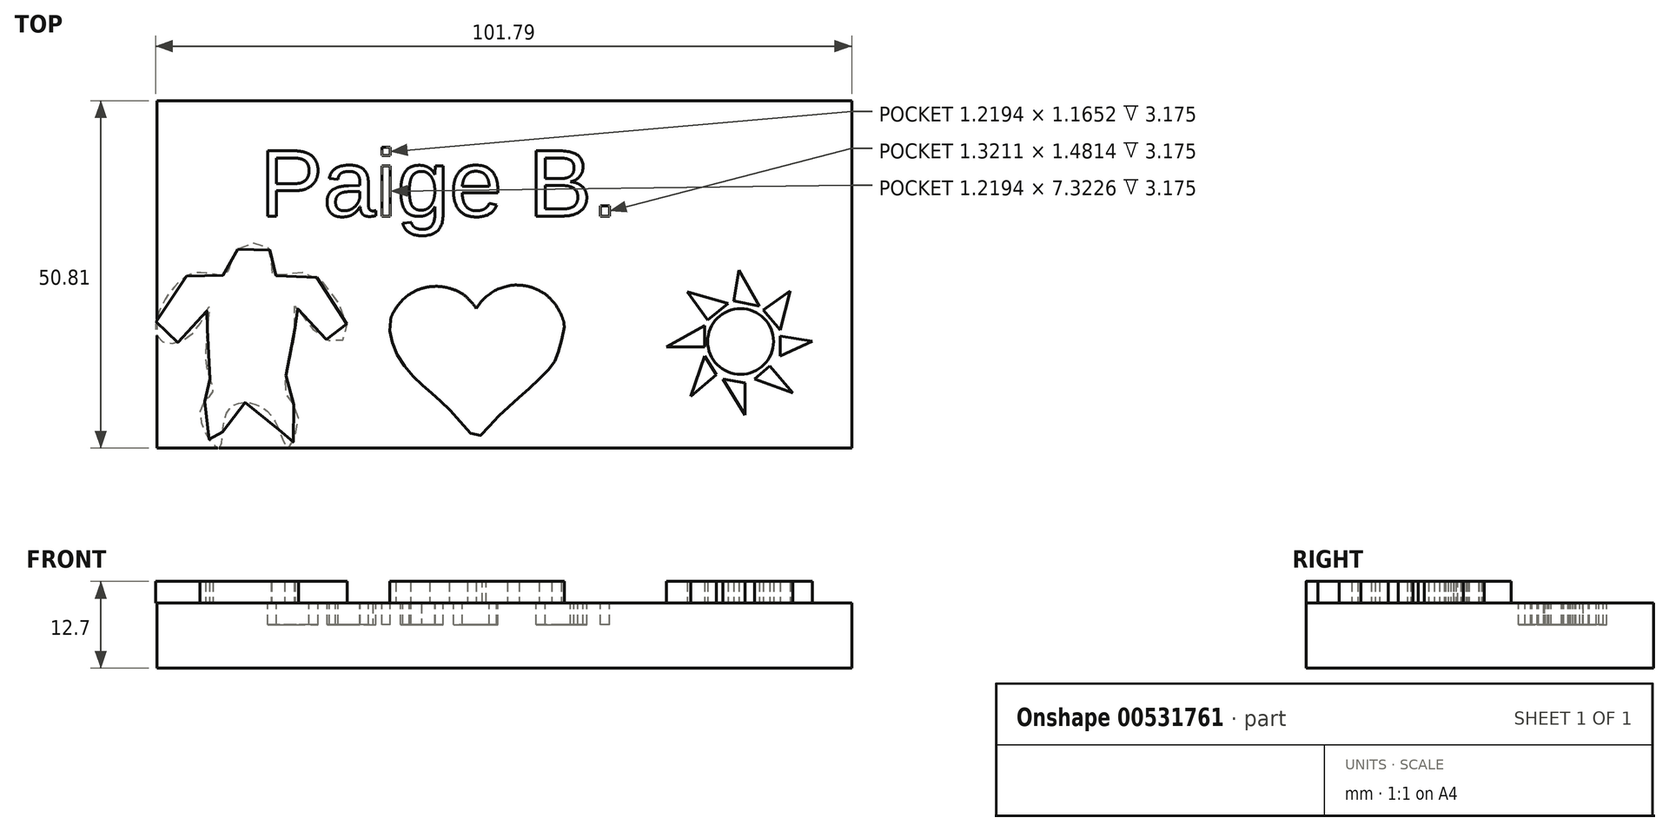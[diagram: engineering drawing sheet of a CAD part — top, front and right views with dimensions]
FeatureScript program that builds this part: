
annotation { "Feature Type Name" : "Feature", "Feature Type Description" : "" }
export const myFeature = defineFeature(function(context is Context, id is Id, definition is map)
    precondition{}
    {
        {
            var Q0;
            Q0=qCreatedBy(makeId("Top.planeOp"),FACE);
            var sketch = newSketch(context, id + "F0", { "sketchPlane" : qUnion([Q0])});
            skLineSegment(sketch, "E0.bottom", {"start": v(-50.8, 25.4) * mm, "end": v(50.8, 25.4) * mm});
            skLineSegment(sketch, "E0.top", {"start": v(-50.8, -25.4) * mm, "end": v(50.8, -25.4) * mm});
            skLineSegment(sketch, "E0.left", {"start": v(-50.8, 25.4) * mm, "end": v(-50.8, -25.4) * mm});
            skLineSegment(sketch, "E0.right", {"start": v(50.8, 25.4) * mm, "end": v(50.8, -25.4) * mm});
            skPoint(sketch, "E0.middle", {"position": v(0, 0) * mm});
            skSolve(sketch);
        }
        {
            var Q0;
            Q0=makeQuery(id+"F0.imprint","IMPRINT",FACE,{"disambiguationData":[TD([[makeQuery(id+"F0.imprint","IMPRINT",EDGE,{"derivedFrom":sQuery(id+"F0.wireOp",EDGE,"E0.bottom")}),-1.0]])]});
            extrude(context, id + "F1", {"entities" : qUnion([Q0]), "depth" : 9.52 * mm, "offsetDistance" : 25.4 * mm});
        }
        {
            var Q0;
            Q0=makeQuery(id+"F1.opExtrude","CAP_FACE",FACE,{"disambiguationData":[OSD([sQuery(id+"F0.wireOp",EDGE,"E0.bottom"),sQuery(id+"F0.wireOp",EDGE,"E0.top"),sQuery(id+"F0.wireOp",EDGE,"E0.left"),sQuery(id+"F0.wireOp",EDGE,"E0.right")])],"isStart":false});
            var sketch = newSketch(context, id + "F2", { "sketchPlane" : qUnion([Q0])});
            skPoint(sketch, "E1.4.internal.snap0", {"position": v(-50.8, -8.96) * mm});
            skPoint(sketch, "E1.15.internal.snap0", {"position": v(-50.8, -8.96) * mm});
            skPoint(sketch, "E1.17.internal.snap0", {"position": v(-23.09, -8.96) * mm});
            skFitSpline(sketch, "E1", {"points": [v(-38.94, 3.7) * mm, v(-40.8, 0) * mm, v(-45.88, 0) * mm, v(-50.8, -8.96) * mm, v(-45.88, -8.96) * mm, v(-43.1, -4.62) * mm, v(-43.57, -13.41) * mm, v(-42.64, -17.11) * mm, v(-44.5, -20.35) * mm, v(-41.72, -25.4) * mm, v(-40.33, -19.89) * mm, v(-34.32, -20.35) * mm, v(-31.54, -25.4) * mm, v(-30.16, -20.35) * mm, v(-32, -17.11) * mm, v(-30.62, -8.96) * mm, v(-30.62, -4.62) * mm, v(-26.92, -8.96) * mm, v(-23.09, -8.96) * mm, v(-28.3, 0) * mm, v(-33.86, 0) * mm, v(-34.32, 3.7) * mm, v(-38.94, 3.7) * mm]});
            skSolve(sketch);
        }
        {
            var Q0;
            {var subQ0=sQuery(id+"F2.wireOp",EDGE,"E1");var subQ1=makeQuery(id+"F1.opExtrude","CAP_EDGE",EDGE,{"disambiguationData":[OSD([sQuery(id+"F0.wireOp",EDGE,"E0.left")])],"isStart":false});var subQ2=makeQuery(id+"F2.imprint","INTERSECT",VERTEX,{"disambiguationData":[OD(0.0)],"derivedFrom":[subQ1,subQ0]});Q0=makeQuery(id+"F2.imprint","IMPRINT",FACE,{"disambiguationData":[TD([[makeQuery(id+"F2.imprint","IMPRINT",EDGE,{"disambiguationData":[TD([[subQ2,1.0]])],"derivedFrom":subQ0}),1.0]])]});}
            var Q1;
            {var subQ0=sQuery(id+"F2.wireOp",EDGE,"E1");var subQ1=makeQuery(id+"F1.opExtrude","CAP_EDGE",EDGE,{"disambiguationData":[OSD([sQuery(id+"F0.wireOp",EDGE,"E0.top")])],"isStart":false});var subQ2=makeQuery(id+"F2.imprint","INTERSECT",VERTEX,{"disambiguationData":[OD(0.0)],"derivedFrom":[subQ1,subQ0]});Q1=makeQuery(id+"F2.imprint","IMPRINT",FACE,{"disambiguationData":[TD([[makeQuery(id+"F2.imprint","IMPRINT",EDGE,{"disambiguationData":[TD([[subQ2,-1.0]])],"derivedFrom":subQ0}),1.0]])]});}
            var Q2;
            {var subQ0=sQuery(id+"F2.wireOp",EDGE,"E1");var subQ1=makeQuery(id+"F1.opExtrude","CAP_EDGE",EDGE,{"disambiguationData":[OSD([sQuery(id+"F0.wireOp",EDGE,"E0.top")])],"isStart":false});var subQ2=makeQuery(id+"F2.imprint","INTERSECT",VERTEX,{"disambiguationData":[OD(2.0)],"derivedFrom":[subQ1,subQ0]});Q2=makeQuery(id+"F2.imprint","IMPRINT",FACE,{"disambiguationData":[TD([[makeQuery(id+"F2.imprint","IMPRINT",EDGE,{"disambiguationData":[TD([[subQ2,-1.0]])],"derivedFrom":subQ0}),1.0]])]});}
            var Q3;
            {var subQ0=sQuery(id+"F2.wireOp",EDGE,"E1");var subQ1=makeQuery(id+"F1.opExtrude","CAP_EDGE",EDGE,{"disambiguationData":[OSD([sQuery(id+"F0.wireOp",EDGE,"E0.left")])],"isStart":false});var subQ5=makeQuery(id+"F2.imprint","INTERSECT",VERTEX,{"disambiguationData":[OD(0.0)],"derivedFrom":[subQ1,subQ0]});Q3=makeQuery(id+"F2.imprint","IMPRINT",FACE,{"disambiguationData":[TD([[makeQuery(id+"F2.imprint","IMPRINT",EDGE,{"disambiguationData":[TD([[subQ5,-1.0]])],"derivedFrom":subQ0}),1.0]])]});}
            extrude(context, id + "F3", {"entities" : qUnion([Q0, Q1, Q2, Q3]), "operationType" : NewBodyOperationType.ADD, "depth" : 3.17 * mm, "offsetDistance" : 25.4 * mm});
        }
        {
            var Q0;
            {var subQ0=sQuery(id+"F0.wireOp",EDGE,"E0.left");var subQ1=makeQuery(id+"F1.opExtrude","SWEPT_FACE",FACE,{"disambiguationData":[OSD([subQ0])]});var subQ2=sQuery(id+"F0.wireOp",EDGE,"E0.top");var subQ3=makeQuery(id+"F1.opExtrude","SWEPT_FACE",FACE,{"disambiguationData":[OSD([subQ2])]});var subQ4=sQuery(id+"F0.wireOp",EDGE,"E0.right");var subQ5=makeQuery(id+"F1.opExtrude","SWEPT_FACE",FACE,{"disambiguationData":[OSD([subQ4])]});var subQ6=sQuery(id+"F0.wireOp",EDGE,"E0.bottom");var subQ7=makeQuery(id+"F1.opExtrude","SWEPT_FACE",FACE,{"disambiguationData":[OSD([subQ6])]});var subQ8=sQuery(id+"F2.wireOp",EDGE,"E1");var subQ9=makeQuery(id+"F3.opExtrude","SWEPT_FACE",FACE,{"disambiguationData":[OSD([subQ8])]});var subQ10=makeQuery(id+"F3.opExtrude","CAP_FACE",FACE,{"disambiguationData":[OSD([subQ8])],"isStart":true});var subQ11=sQuery(id+"F7vCEPkGthSsVVi_1.wireOp",EDGE,"900b0a7b-35fd-46bd-af1a-971b247ca61f");Q0=makeQuery(id+"FpG3tMiEOksPE03_1.boolean.opBoolean","SPLIT",FACE,{"disambiguationData":[TD([subQ7,subQ3,subQ1,subQ5,subQ9,subQ10,makeQuery(id+"FpG3tMiEOksPE03_1.opExtrude","SWEPT_FACE",FACE,{"disambiguationData":[OSD([subQ11])]}),makeQuery(id+"FpG3tMiEOksPE03_1.opExtrude","CAP_FACE",FACE,{"disambiguationData":[OSD([subQ2,subQ11])],"isStart":true}),makeQuery(id+"FpG3tMiEOksPE03_1.opExtrude","SWEPT_FACE",FACE,{"disambiguationData":[OSD([subQ2])]})])],"derivedFrom":makeQuery(id+"F3.boolean.opBoolean","SPLIT",FACE,{"disambiguationData":[TD([subQ7,subQ3,subQ1,subQ5,subQ9,subQ10])],"derivedFrom":makeQuery(id+"F1.opExtrude","CAP_FACE",FACE,{"disambiguationData":[OSD([subQ6,subQ2,subQ0,subQ4])],"isStart":false})})});}
            var sketch = newSketch(context, id + "F4", { "sketchPlane" : qUnion([Q0])});
            skText(sketch, "E2", { "text": "Paige B.", "fontName": "Arimo-Regular.ttf"});
            const initialGuessF4  = {"E2": [-0.03574, 0.00853, 1, 0, 0.00998]};
            skSetInitialGuess(sketch, initialGuessF4);
            skSolve(sketch);
        }
        {
            var Q0;
            Q0 = qSketchRegion(id + "F4", true);
            extrude(context, id + "F5", {"entities" : qUnion([Q0]), "operationType" : NewBodyOperationType.REMOVE, "oppositeDirection" : true, "depth" : 3.17 * mm, "offsetDistance" : 25.4 * mm});
        }
        {
            var Q0;
            {var subQ0=sQuery(id+"F0.wireOp",EDGE,"E0.right");var subQ1=makeQuery(id+"F1.opExtrude","SWEPT_FACE",FACE,{"disambiguationData":[OSD([subQ0])]});var subQ2=sQuery(id+"F0.wireOp",EDGE,"E0.left");var subQ3=makeQuery(id+"F1.opExtrude","SWEPT_FACE",FACE,{"disambiguationData":[OSD([subQ2])]});var subQ4=sQuery(id+"F0.wireOp",EDGE,"E0.top");var subQ5=makeQuery(id+"F1.opExtrude","SWEPT_FACE",FACE,{"disambiguationData":[OSD([subQ4])]});var subQ6=sQuery(id+"F0.wireOp",EDGE,"E0.bottom");var subQ7=makeQuery(id+"F1.opExtrude","SWEPT_FACE",FACE,{"disambiguationData":[OSD([subQ6])]});var subQ8=sQuery(id+"F2.wireOp",EDGE,"E1");var subQ9=makeQuery(id+"F3.opExtrude","SWEPT_FACE",FACE,{"disambiguationData":[OSD([subQ8])]});var subQ10=makeQuery(id+"F3.opExtrude","CAP_FACE",FACE,{"disambiguationData":[OSD([subQ8])],"isStart":true});var subQ11=sQuery(id+"F7vCEPkGthSsVVi_1.wireOp",EDGE,"900b0a7b-35fd-46bd-af1a-971b247ca61f");var subQ12=makeQuery(id+"FpG3tMiEOksPE03_1.opExtrude","SWEPT_FACE",FACE,{"disambiguationData":[OSD([subQ11])]});var subQ13=makeQuery(id+"FpG3tMiEOksPE03_1.opExtrude","CAP_FACE",FACE,{"disambiguationData":[OSD([subQ4,subQ11])],"isStart":true});var subQ14=makeQuery(id+"FpG3tMiEOksPE03_1.opExtrude","SWEPT_FACE",FACE,{"disambiguationData":[OSD([subQ4])]});Q0=makeQuery(id+"F5.boolean.opBoolean","SPLIT",FACE,{"disambiguationData":[TD([subQ7])],"derivedFrom":makeQuery(id+"FpG3tMiEOksPE03_1.boolean.opBoolean","SPLIT",FACE,{"disambiguationData":[TD([subQ7,subQ5,subQ3,subQ1,subQ9,subQ10,subQ12,subQ13,subQ14])],"derivedFrom":makeQuery(id+"F3.boolean.opBoolean","SPLIT",FACE,{"disambiguationData":[TD([subQ7,subQ5,subQ3,subQ1,subQ9,subQ10])],"derivedFrom":makeQuery(id+"F1.opExtrude","CAP_FACE",FACE,{"disambiguationData":[OSD([subQ6,subQ4,subQ2,subQ0])],"isStart":false})})})});}
            var sketch = newSketch(context, id + "F6", { "sketchPlane" : qUnion([Q0])});
            skArc(sketch, "E3", {"start": v(-4.08, -5) * mm, "mid": v(-10.9, -1.81) * mm, "end": v(-16.64, -6.7) * mm});
            skArc(sketch, "E4", {"start": v(8.76, -7.7) * mm, "mid": v(3.31, -1.72) * mm, "end": v(-4.08, -5) * mm});
            skPoint(sketch, "E5.12.internal.snap0", {"position": v(8.76, -12.7) * mm});
            skPoint(sketch, "E5.20.internal.snap0", {"position": v(3.31, -1.72) * mm});
            skFitSpline(sketch, "E5", {"points": [v(-16.64, -6.7) * mm, v(-16.64, -8.9) * mm, v(-15.6, -11.83) * mm, v(-13.57, -14.67) * mm, v(-11.3, -16.79) * mm, v(-9.26, -18.58) * mm, v(-6.74, -21.18) * mm, v(-3.98, -23.7) * mm, v(-1.94, -21.91) * mm, v(0.66, -19.4) * mm, v(3.26, -17.03) * mm, v(5.95, -14.51) * mm, v(7.41, -12.7) * mm, v(8.06, -10.85) * mm, v(8.76, -7.7) * mm, v(8.32, -5.93) * mm, v(6.98, -3.8) * mm, v(5.1, -2.36) * mm, v(3.31, -1.72) * mm, v(2.21, -1.58) * mm, v(0.48, -1.72) * mm, v(-3.2, -3.82) * mm, v(-4.08, -5) * mm, v(-5.36, -3.5) * mm, v(-8.03, -2.03) * mm, v(-10.9, -1.81) * mm, v(-13.65, -2.8) * mm, v(-15.86, -5) * mm, v(-16.64, -6.7) * mm]});
            skSolve(sketch);
        }
        {
            var Q0;
            Q0 = qSketchRegion(id + "F6", true);
            extrude(context, id + "F7", {"entities" : qUnion([Q0]), "operationType" : NewBodyOperationType.ADD, "depth" : 3.17 * mm, "offsetDistance" : 25.4 * mm});
        }
        {
            var Q0;
            {var subQ0=sQuery(id+"F0.wireOp",EDGE,"E0.bottom");var subQ1=makeQuery(id+"F1.opExtrude","SWEPT_FACE",FACE,{"disambiguationData":[OSD([subQ0])]});var subQ2=sQuery(id+"F2.wireOp",EDGE,"E1");var subQ3=makeQuery(id+"F3.opExtrude","SWEPT_FACE",FACE,{"disambiguationData":[OSD([subQ2])]});var subQ4=sQuery(id+"F0.wireOp",EDGE,"E0.right");var subQ5=makeQuery(id+"F1.opExtrude","SWEPT_FACE",FACE,{"disambiguationData":[OSD([subQ4])]});var subQ6=makeQuery(id+"F3.opExtrude","CAP_FACE",FACE,{"disambiguationData":[OSD([subQ2])],"isStart":true});var subQ7=sQuery(id+"F0.wireOp",EDGE,"E0.top");var subQ8=makeQuery(id+"F1.opExtrude","SWEPT_FACE",FACE,{"disambiguationData":[OSD([subQ7])]});var subQ9=sQuery(id+"F0.wireOp",EDGE,"E0.left");var subQ10=makeQuery(id+"F1.opExtrude","SWEPT_FACE",FACE,{"disambiguationData":[OSD([subQ9])]});Q0=makeQuery(id+"F5.boolean.opBoolean","SPLIT",FACE,{"disambiguationData":[TD([subQ1])],"derivedFrom":makeQuery(id+"F3.boolean.opBoolean","SPLIT",FACE,{"disambiguationData":[TD([subQ1,subQ8,subQ10,subQ5,subQ3,subQ6])],"derivedFrom":makeQuery(id+"F1.opExtrude","CAP_FACE",FACE,{"disambiguationData":[OSD([subQ0,subQ7,subQ9,subQ4])],"isStart":false})})});}
            var sketch = newSketch(context, id + "F8", { "sketchPlane" : qUnion([Q0])});
            skCircle(sketch, "E6", {"center": v(34.56, -9.82) * mm, "radius": 4.81 * mm});
            skLineSegment(sketch, "E7", {"start": v(33.6, -3.85) * mm, "end": v(37.29, -4.63) * mm});
            skLineSegment(sketch, "E8", {"start": v(37.29, -4.63) * mm, "end": v(34.3, 0.63) * mm});
            skLineSegment(sketch, "E9", {"start": v(34.3, 0.63) * mm, "end": v(33.6, -3.85) * mm});
            skLineSegment(sketch, "E10", {"start": v(32.74, -4.28) * mm, "end": v(26.8, -2.54) * mm});
            skLineSegment(sketch, "E11", {"start": v(26.8, -2.54) * mm, "end": v(29.75, -6.7) * mm});
            skLineSegment(sketch, "E12", {"start": v(29.75, -6.7) * mm, "end": v(32.74, -4.28) * mm});
            skLineSegment(sketch, "E13", {"start": v(29.32, -7.48) * mm, "end": v(29.32, -10.6) * mm});
            skLineSegment(sketch, "E14", {"start": v(29.32, -10.6) * mm, "end": v(23.7, -10.6) * mm});
            skLineSegment(sketch, "E15", {"start": v(23.7, -10.6) * mm, "end": v(29.32, -7.48) * mm});
            skLineSegment(sketch, "E16", {"start": v(29.32, -11.96) * mm, "end": v(31.03, -14.66) * mm});
            skLineSegment(sketch, "E17", {"start": v(31.03, -14.66) * mm, "end": v(27.26, -17.86) * mm});
            skLineSegment(sketch, "E18", {"start": v(27.26, -17.86) * mm, "end": v(29.32, -11.96) * mm});
            skLineSegment(sketch, "E19", {"start": v(31.95, -15.3) * mm, "end": v(35.23, -15.87) * mm});
            skLineSegment(sketch, "E20", {"start": v(35.23, -15.87) * mm, "end": v(35.23, -20.56) * mm});
            skLineSegment(sketch, "E21", {"start": v(35.23, -20.56) * mm, "end": v(31.95, -15.3) * mm});
            skLineSegment(sketch, "E22", {"start": v(36.58, -15.3) * mm, "end": v(38.84, -13.38) * mm});
            skLineSegment(sketch, "E23", {"start": v(38.84, -13.38) * mm, "end": v(42.22, -17.37) * mm});
            skLineSegment(sketch, "E24", {"start": v(42.22, -17.37) * mm, "end": v(36.58, -15.3) * mm});
            skLineSegment(sketch, "E25", {"start": v(40.35, -9.04) * mm, "end": v(40.35, -11.96) * mm});
            skLineSegment(sketch, "E26", {"start": v(40.35, -11.96) * mm, "end": v(45.04, -9.75) * mm});
            skLineSegment(sketch, "E27", {"start": v(45.04, -9.75) * mm, "end": v(40.35, -9.04) * mm});
            skLineSegment(sketch, "E28", {"start": v(37.86, -5.2) * mm, "end": v(40.35, -8.13) * mm});
            skLineSegment(sketch, "E29", {"start": v(40.35, -8.13) * mm, "end": v(41.84, -2.43) * mm});
            skLineSegment(sketch, "E30", {"start": v(41.84, -2.43) * mm, "end": v(37.86, -5.2) * mm});
            skSolve(sketch);
        }
        {
            var Q0;
            Q0=makeQuery(id+"F8.imprint","IMPRINT",FACE,{"disambiguationData":[TD([[makeQuery(id+"F8.imprint","IMPRINT",EDGE,{"derivedFrom":sQuery(id+"F8.wireOp",EDGE,"E13")}),-1.0]])]});
            var Q1;
            Q1=makeQuery(id+"F8.imprint","IMPRINT",FACE,{"disambiguationData":[TD([[makeQuery(id+"F8.imprint","IMPRINT",EDGE,{"derivedFrom":sQuery(id+"F8.wireOp",EDGE,"E28")}),1.0]])]});
            var Q2;
            Q2=makeQuery(id+"F8.imprint","IMPRINT",FACE,{"disambiguationData":[TD([[makeQuery(id+"F8.imprint","IMPRINT",EDGE,{"derivedFrom":sQuery(id+"F8.wireOp",EDGE,"E10")}),1.0]])]});
            var Q3;
            Q3=makeQuery(id+"F8.imprint","IMPRINT",FACE,{"disambiguationData":[TD([[makeQuery(id+"F8.imprint","IMPRINT",EDGE,{"derivedFrom":sQuery(id+"F8.wireOp",EDGE,"E25")}),1.0]])]});
            var Q4;
            Q4=makeQuery(id+"F8.imprint","IMPRINT",FACE,{"disambiguationData":[TD([[makeQuery(id+"F8.imprint","IMPRINT",EDGE,{"derivedFrom":sQuery(id+"F8.wireOp",EDGE,"E7")}),1.0]])]});
            var Q5;
            Q5=makeQuery(id+"F8.imprint","IMPRINT",FACE,{"disambiguationData":[TD([[makeQuery(id+"F8.imprint","IMPRINT",EDGE,{"derivedFrom":sQuery(id+"F8.wireOp",EDGE,"E22")}),-1.0]])]});
            var Q6;
            Q6=makeQuery(id+"F8.imprint","IMPRINT",FACE,{"disambiguationData":[TD([[makeQuery(id+"F8.imprint","IMPRINT",EDGE,{"derivedFrom":sQuery(id+"F8.wireOp",EDGE,"E16")}),-1.0]])]});
            var Q7;
            Q7=makeQuery(id+"F8.imprint","IMPRINT",FACE,{"disambiguationData":[TD([[makeQuery(id+"F8.imprint","IMPRINT",EDGE,{"derivedFrom":sQuery(id+"F8.wireOp",EDGE,"E19")}),-1.0]])]});
            var Q8;
            Q8=makeQuery(id+"F8.imprint","IMPRINT",FACE,{"disambiguationData":[TD([[makeQuery(id+"F8.imprint","IMPRINT",EDGE,{"derivedFrom":sQuery(id+"F8.wireOp",EDGE,"E6")}),1.0]])]});
            extrude(context, id + "F9", {"entities" : qUnion([Q0, Q1, Q2, Q3, Q4, Q5, Q6, Q7, Q8]), "operationType" : NewBodyOperationType.ADD, "depth" : 3.17 * mm, "offsetDistance" : 25.4 * mm});
        }
    });
